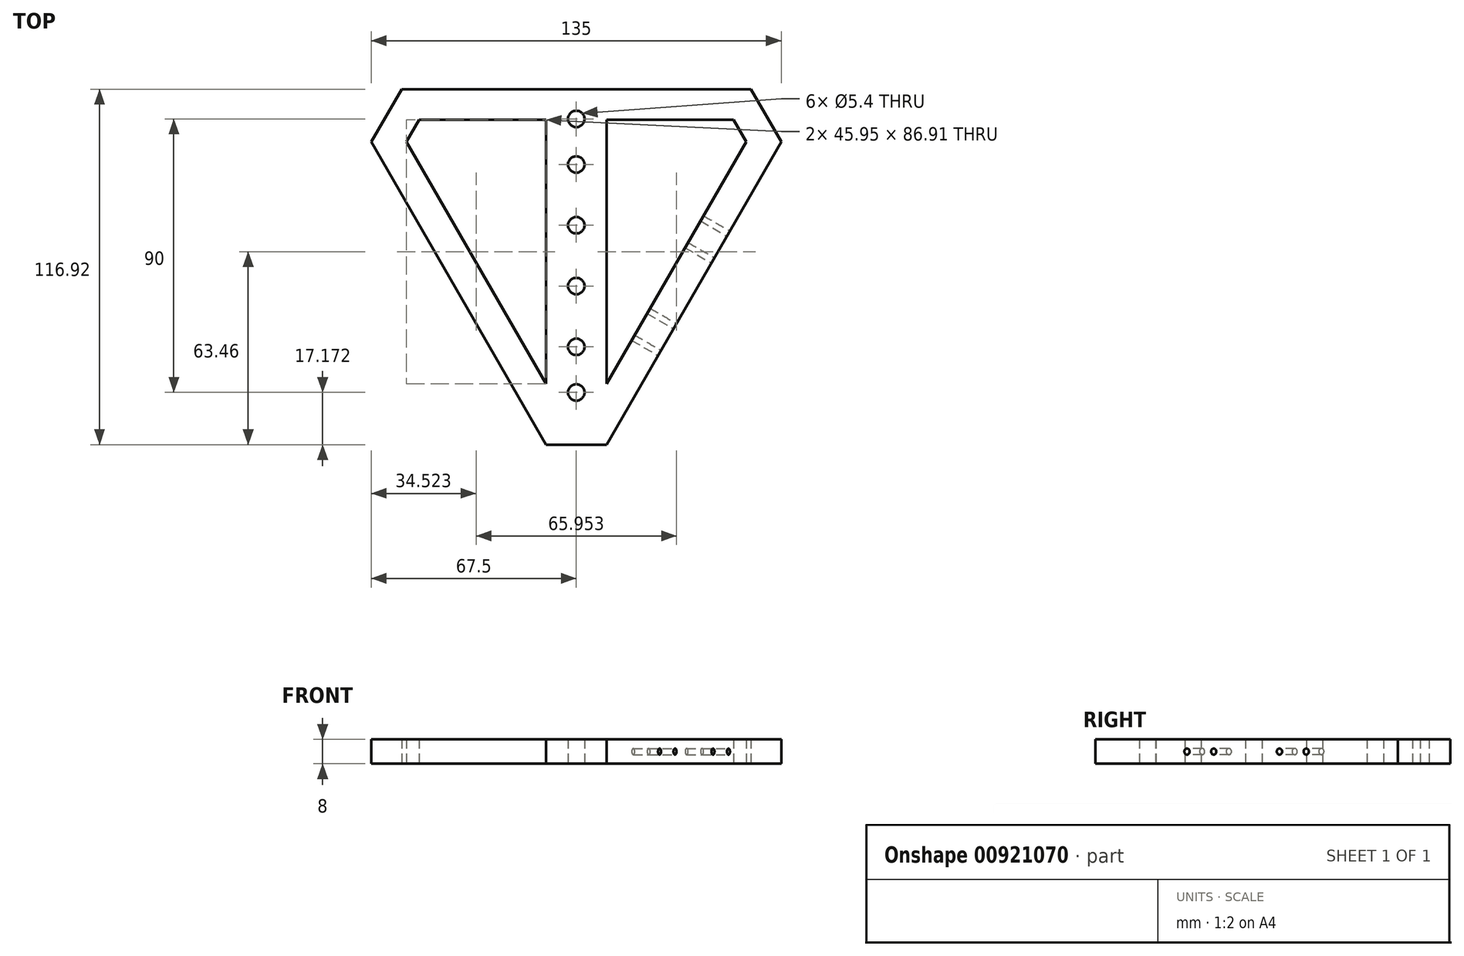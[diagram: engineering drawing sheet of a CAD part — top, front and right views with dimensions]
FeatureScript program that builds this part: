
annotation { "Feature Type Name" : "Feature", "Feature Type Description" : "" }
export const myFeature = defineFeature(function(context is Context, id is Id, definition is map)
    precondition{}
    {
        {
            var Q0;
            Q0=qCreatedBy(makeId("Top.planeOp"),FACE);
            var sketch = newSketch(context, id + "F0", { "sketchPlane" : qUnion([Q0])});
            skLineSegment(sketch, "E0", {"start": v(-57.5, 58.46) * mm, "end": v(57.5, 58.46) * mm});
            skLineSegment(sketch, "E1", {"start": v(57.5, 58.46) * mm, "end": v(67.5, 41.14) * mm});
            skLineSegment(sketch, "E2", {"start": v(67.5, 41.14) * mm, "end": v(10, -58.46) * mm});
            skLineSegment(sketch, "E3", {"start": v(10, -58.46) * mm, "end": v(-10, -58.46) * mm});
            skLineSegment(sketch, "E4", {"start": v(-10, -58.46) * mm, "end": v(-67.5, 41.14) * mm});
            skLineSegment(sketch, "E5", {"start": v(-67.5, 41.14) * mm, "end": v(-57.5, 58.46) * mm});
            skLineSegment(sketch, "E6", {"start": v(0, 58.46) * mm, "end": v(0, -58.46) * mm, "construction": true});
            skPoint(sketch, "E7", {"position": v(0, 0) * mm});
            skLineSegment(sketch, "E8.0", {"start": v(55.95, 41.14) * mm, "end": v(4.23, -48.46) * mm});
            skLineSegment(sketch, "E8.1", {"start": v(-4.23, -48.46) * mm, "end": v(-55.95, 41.14) * mm});
            skLineSegment(sketch, "E8.2", {"start": v(-55.95, 41.14) * mm, "end": v(-51.73, 48.46) * mm});
            skLineSegment(sketch, "E8.3", {"start": v(4.23, -48.46) * mm, "end": v(-4.23, -48.46) * mm});
            skLineSegment(sketch, "E8.4", {"start": v(-51.73, 48.46) * mm, "end": v(-10, 48.46) * mm});
            skLineSegment(sketch, "E8.5", {"start": v(51.73, 48.46) * mm, "end": v(55.95, 41.14) * mm});
            skLineSegment(sketch, "E9.left", {"start": v(10, 48.46) * mm, "end": v(10, -38.46) * mm});
            skLineSegment(sketch, "E9.right", {"start": v(-10, 48.46) * mm, "end": v(-10, -38.46) * mm});
            skCircle(sketch, "E10", {"center": v(0, 33.71) * mm, "radius": 2.7 * mm});
            skCircle(sketch, "E11", {"center": v(0, -6.29) * mm, "radius": 2.7 * mm});
            skCircle(sketch, "E12", {"center": v(0, 48.71) * mm, "radius": 2.7 * mm});
            skCircle(sketch, "E13", {"center": v(0, -26.29) * mm, "radius": 2.7 * mm});
            skLineSegment(sketch, "E14.trimOffspring", {"start": v(10, 48.46) * mm, "end": v(51.73, 48.46) * mm});
            skPoint(sketch, "E15.orphan", {"position": v(-10, -48.46) * mm});
            skPoint(sketch, "E16.orphan", {"position": v(10, -48.46) * mm});
            skLineSegment(sketch, "E17", {"start": v(38.75, -8.66) * mm, "end": v(-62.5, 49.8) * mm, "construction": true});
            skLineSegment(sketch, "E18", {"start": v(-38.75, -8.66) * mm, "end": v(62.5, 49.8) * mm, "construction": true});
            skCircle(sketch, "E19", {"center": v(0, 13.71) * mm, "radius": 2.7 * mm});
            skCircle(sketch, "E20", {"center": v(0, -41.29) * mm, "radius": 2.7 * mm});
            skSolve(sketch);
        }
        {
            var Q0;
            Q0 = qSketchRegion(id + "F0", true);
            extrude(context, id + "F1", {"entities" : qUnion([Q0]), "depth" : 8 * mm, "offsetDistance" : 25 * mm});
        }
        {
            var Q0;
            Q0=makeQuery(id+"F1.opExtrude","SWEPT_FACE",FACE,{"disambiguationData":[OSD([sQuery(id+"F0.wireOp",EDGE,"E2")])]});
            var sketch = newSketch(context, id + "F2", { "sketchPlane" : qUnion([Q0])});
            skLineSegment(sketch, "E21", {"start": v(-45.62, 4) * mm, "end": v(69.38, 4) * mm, "construction": true});
            skLineSegment(sketch, "E22", {"start": v(11.87, 0) * mm, "end": v(11.87, 8) * mm, "construction": true});
            skCircle(sketch, "E23", {"center": v(-10.8, 4) * mm, "radius": 1 * mm});
            skCircle(sketch, "E24", {"center": v(-0.62, 4) * mm, "radius": 1 * mm});
            skCircle(sketch, "E25.MirrorC", {"center": v(34.55, 4) * mm, "radius": 1 * mm});
            skCircle(sketch, "E26.MirrorC", {"center": v(24.38, 4) * mm, "radius": 1 * mm});
            skSolve(sketch);
        }
        {
            var Q0;
            Q0 = qSketchRegion(id + "F2", true);
            extrude(context, id + "F3", {"entities" : qUnion([Q0]), "operationType" : NewBodyOperationType.REMOVE, "oppositeDirection" : true, "depth" : 11 * mm, "offsetDistance" : 25 * mm});
        }
    });
